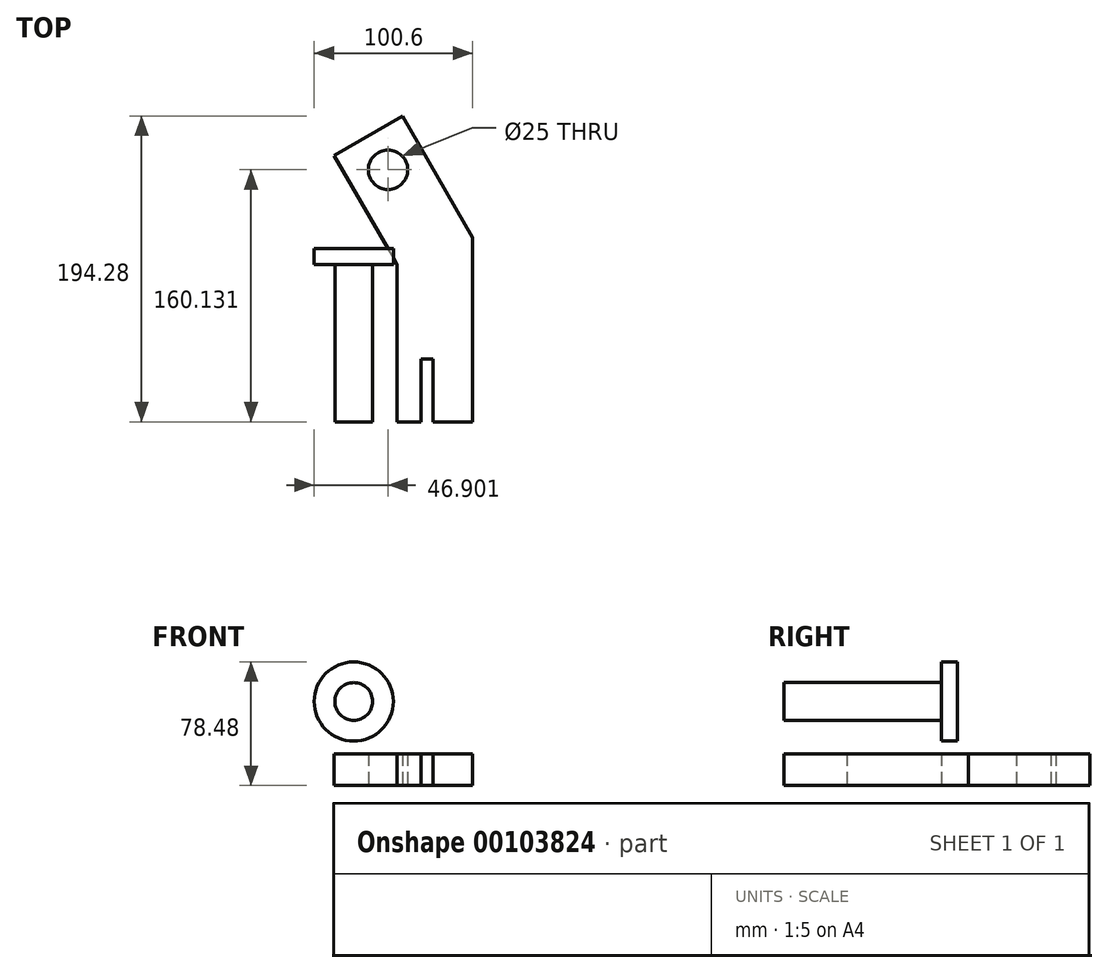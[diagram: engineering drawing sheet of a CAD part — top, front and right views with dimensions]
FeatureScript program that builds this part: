
annotation { "Feature Type Name" : "Feature", "Feature Type Description" : "" }
export const myFeature = defineFeature(function(context is Context, id is Id, definition is map)
    precondition{}
    {
        {
            var Q0;
            Q0=qCreatedBy(makeId("Top.planeOp"),FACE);
            var sketch = newSketch(context, id + "F0", { "sketchPlane" : qUnion([Q0])});
            skLineSegment(sketch, "E0", {"start": v(0, 0) * mm, "end": v(0, 100) * mm});
            skLineSegment(sketch, "E1", {"start": v(0, 100) * mm, "end": v(-40, 169.28) * mm});
            skLineSegment(sketch, "E2", {"start": v(-40, 169.28) * mm, "end": v(3.3, 194.28) * mm});
            skLineSegment(sketch, "E3", {"start": v(3.3, 194.28) * mm, "end": v(47.85, 117.12) * mm});
            skLineSegment(sketch, "E4", {"start": v(47.85, 117.12) * mm, "end": v(47.85, 0) * mm});
            skCircle(sketch, "E5", {"center": v(-5.85, 160.13) * mm, "radius": 12.5 * mm});
            skLineSegment(sketch, "E6", {"start": v(15, 0) * mm, "end": v(15, 40) * mm});
            skLineSegment(sketch, "E7", {"start": v(15, 40) * mm, "end": v(22.85, 40) * mm});
            skLineSegment(sketch, "E8", {"start": v(22.85, 40) * mm, "end": v(22.85, 0) * mm});
            skLineSegment(sketch, "E9", {"start": v(0, 0) * mm, "end": v(15, 0) * mm});
            skLineSegment(sketch, "E10", {"start": v(22.85, 0) * mm, "end": v(47.85, 0) * mm});
            skSolve(sketch);
        }
        {
            var Q0;
            Q0=makeQuery(id+"F0.imprint","IMPRINT",FACE,{"disambiguationData":[TD([[makeQuery(id+"F0.imprint","IMPRINT",EDGE,{"derivedFrom":sQuery(id+"F0.wireOp",EDGE,"E0")}),-1.0]])]});
            extrude(context, id + "F1", {"entities" : qUnion([Q0]), "depth" : 20 * mm});
        }
        {
            var Q0;
            Q0=qCreatedBy(makeId("Front.planeOp"),FACE);
            var sketch = newSketch(context, id + "F2", { "sketchPlane" : qUnion([Q0])});
            skCircle(sketch, "E11", {"center": v(-27.62, 53.36) * mm, "radius": 12 * mm});
            skSolve(sketch);
        }
        {
            var Q0;
            Q0=makeQuery(id+"F2.imprint","IMPRINT",FACE,{"disambiguationData":[TD([[makeQuery(id+"F2.imprint","IMPRINT",EDGE,{"derivedFrom":sQuery(id+"F2.wireOp",EDGE,"E11")}),1.0]])]});
            extrude(context, id + "F3", {"entities" : qUnion([Q0]), "operationType" : NewBodyOperationType.ADD, "oppositeDirection" : true, "depth" : 100 * mm});
        }
        {
            var Q0;
            Q0=makeQuery(id+"F3.opExtrude","CAP_FACE",FACE,{"disambiguationData":[OSD([sQuery(id+"F2.wireOp",EDGE,"E11")])],"isStart":false});
            var sketch = newSketch(context, id + "F4", { "sketchPlane" : qUnion([Q0])});
            skCircle(sketch, "E12", {"center": v(27.62, 53.36) * mm, "radius": 25.13 * mm});
            skSolve(sketch);
        }
        {
            var Q0;
            Q0 = qSketchRegion(id + "F4", true);
            extrude(context, id + "F5", {"entities" : qUnion([Q0]), "operationType" : NewBodyOperationType.ADD, "depth" : 10 * mm});
        }
    });
